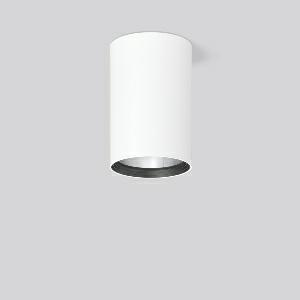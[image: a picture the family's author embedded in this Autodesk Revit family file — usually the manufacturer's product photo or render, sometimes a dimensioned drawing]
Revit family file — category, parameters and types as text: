
# Revit family: heledon_maxi_a_931233_002_76_0a28
name_source: partatom
category: Lighting Fixtures
units: mm (PartAtom-declared; Revit-internal decimal feet)

## family parameters
Cut with Voids When Loaded = No
Host = Face
Light Source = No
Part Type = Normal
Room Calculation Point = No
Round Connector Dimension = Use Diameter
Shared = No

## types (1)
- HELEDON maxi A (1 x LED Modul 932 fresh meat, 2050 lm, 3200)
    Apparent Load = 33 VA
    Approval mark = CE
    CIE Flux Codes = 96 100 100 100 100
    Color Rendering = 90
    Color Temperature = 3200
    Default Elevation = 1800 mm
    Description = Series: HELEDON maxi
Cylindrical surface-mounted downlight. Housing: die-cast aluminium, powder-coated. Internal ceiling frame polycarbonate with bayonet mounting. Black plastic ring and recessed LED to prevent glare from the side. Optical assembly with reflector made of MIRO-Silver with 98% total light reflection for outstanding efficiency - can be changed without tools. Special LED for illumination of meat included. Suitable for Ceiling mounting. Easy installation with a separate ceiling frame with bayonet mounting and plug connection. Driver integrated. Connected via plug-in connector. High quality converter without flickering and stroboscopic effect. The following accessories can be mounted without use of tools: interchangeable lenses, decorative glasses, honeycomb louvre, clear and frosted diffusers, white interchangeable plastic ring. 
Colour: traffic white, matt (RAL 9016)
Diameter: 123 mm
Height: 183 mm
Lamp: LED
Socket: without socket
Colour temperature: fresh meat
System power: 33 W
Rated luminous flux: 2050 lm
Luminous efficiency: 62 lm/W
Control gear: Converter, dimmable, DALI
Protection class: I
Type of protection: IP 20
    Height = 183 mm
    Lamp = 1 x LED Modul 932 fresh meat
    Lamp Light Flux = 2050 lm
    Lamp count = 1
    Length = 123 mm
    Lifetime = 50000 h
    Luminous efficacy = 62 lm/W
    Manufacturer = RZB
    ModVariant = No
    Model = 931233.002.76
    Mounting Place = Ceiling
    Mounting Type = Surface mounted
    Number of Poles = 1
    OnlyDefault = Yes
    Power Factor = 1
    Product Name = HELEDON maxi A
    Product group = Surface mounted downlights
    ProductGroupID = 302
    Protection Class = Protection class I
    Protection Degree = IP 20
    RLX_Detail_Level = 1
    RLX_Emergency_Light_Flux = 0 lm
    RLX_Emergency_Type = 0
    RLX_Emergency_Type_DB = No
    RlxData = <blob elided: 97849 chars, md5=5ce182a9>
    Socket = socket
    Standby Power = 0 W
    System Light Flux = 2050 lm
    System Power = 33 W
    Type Comments = Product without accessories
    Type Image = 931192.002.jpg
    URL = http://relux.com
    VarID = ---
    Voltage = 230 V
    Voltage Range = 220-240 V
    Weight = 0.00 kg
    Width = 0 mm  [stored 0 ft]

note: [stored X ft] marks values corroborated as IEEE doubles in the binary element streams (Revit-internal decimal feet)

## geometry (parser evidence)
native form markers: Blend x4, Sweep x10
no freeform markers — native parametric forms only
